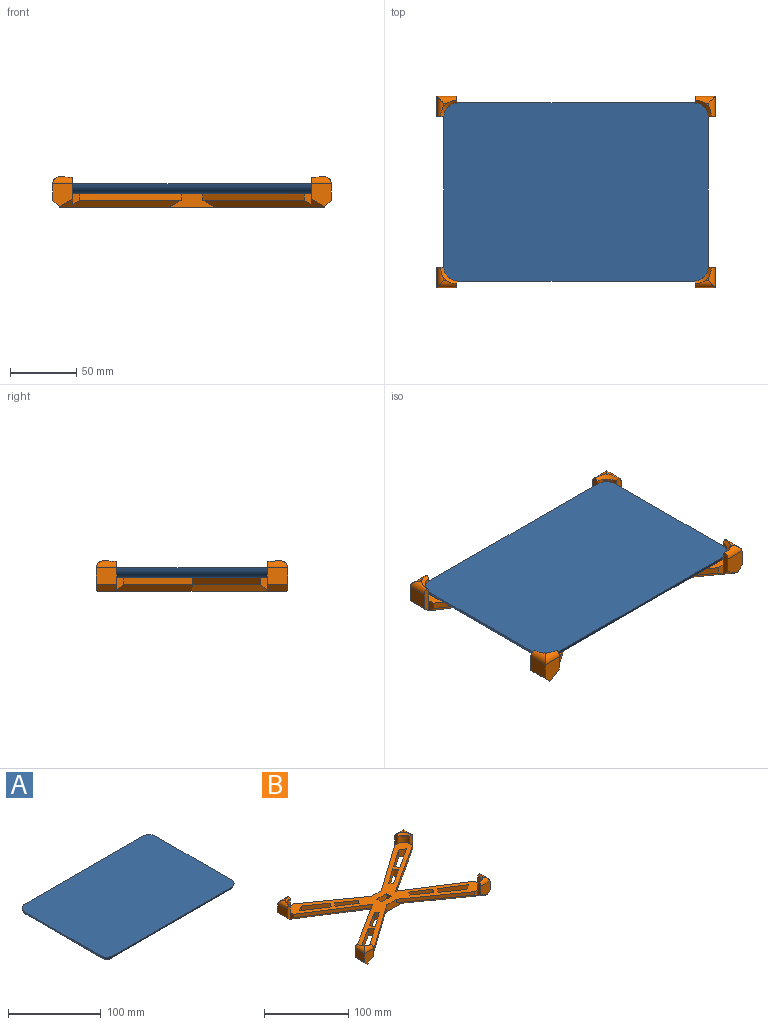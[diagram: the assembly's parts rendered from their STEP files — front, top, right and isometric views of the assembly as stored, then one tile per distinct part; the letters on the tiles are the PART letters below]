
ASSEMBLY  parts=2 mates=1
PART A: 10 faces, bbox 200x135x7.6 mm
  f0: plane 200.03x135mm, normal (0,0,1), area 26920.3mm2, adj f2,f3,f4,f5,f6,f7,f8,f9
  f1: plane 180.35x115.33mm, normal (0,0,-1), area 20798.9mm2, adj f2,f3,f4,f5
  f2: cylinder r=10.16mm len=180.35mm, axis (-1,0,0), area 2415.3mm2, adj f0,f1,f6,f7
  f3: cylinder r=10.16mm len=115.33mm, axis (0,1,0), area 1544.4mm2, adj f0,f1,f6,f8
  f4: cylinder r=10.16mm len=115.33mm, axis (0,1,0), area 1544.4mm2, adj f0,f1,f7,f9
  f5: cylinder r=10.16mm len=180.35mm, axis (-1,0,0), area 2415.3mm2, adj f0,f1,f8,f9
  f6: sphere r=10.16mm, area 121.6mm2, adj f0,f2,f3
  f7: sphere r=10.16mm, area 121.6mm2, adj f0,f2,f4
  f8: sphere r=10.16mm, area 121.6mm2, adj f0,f3,f5
  f9: sphere r=10.16mm, area 121.6mm2, adj f0,f4,f5
PART B: 116 faces, bbox 210.8x144.8x22.9 mm
  f0: plane 200.66x134.62mm, normal (0,0,1), area 6145mm2, adj f1,f2,f3,f4,f5,f6,f7,f8
  f1: plane 10.16x6.11mm, normal (0.82,-0.58,0), area 76.2mm2, adj f0,f2,f70,f71
  f2: plane 32.46x20.8mm, normal (-0.54,-0.84,0), area 391.7mm2, adj f0,f1,f3,f71
  f3: plane 10.16x9.01mm, normal (-0.49,0.87,0), area 105.1mm2, adj f0,f2,f70,f71
  f4: plane 24.65x15.79mm, normal (-0.54,-0.84,0), area 297.4mm2, adj f0,f5,f61,f71
  f5: plane 10.16x5.91mm, normal (-0.82,0.58,0), area 73.6mm2, adj f0,f4,f6,f71
  f6: plane 23.6x16.78mm, normal (0.58,0.82,0), area 294.2mm2, adj f0,f5,f61,f71
  f7: plane 32.59x20.88mm, normal (-0.54,0.84,0), area 393.2mm2, adj f0,f8,f62,f71
  f8: plane 10.16x6.11mm, normal (0.82,0.58,0), area 76.2mm2, adj f0,f7,f9,f71
  f9: plane 27.91x19.84mm, normal (0.58,-0.82,0), area 347.9mm2, adj f0,f8,f62,f71
  f10: plane 10.16x6.11mm, normal (-0.84,-0.54,0), area 73.7mm2, adj f0,f11,f63,f71
  f11: plane 24.53x15.71mm, normal (-0.54,0.84,0), area 295.9mm2, adj f0,f10,f12,f71
  f12: plane 10.16x4.76mm, normal (0.82,0.58,0), area 59.4mm2, adj f0,f11,f63,f71
  f13: plane 10.16x6.31mm, normal (-0.84,0.54,0), area 76.1mm2, adj f0,f14,f64,f71
  f14: plane 32.89x21.07mm, normal (0.54,0.84,0), area 396.9mm2, adj f0,f13,f15,f71
  f15: plane 10.16x9.02mm, normal (0.49,-0.87,0), area 105.2mm2, adj f0,f14,f64,f71
  f16: plane 24.53x15.71mm, normal (0.54,0.84,0), area 295.9mm2, adj f0,f17,f65,f71
  f17: plane 10.16x5.91mm, normal (0.82,-0.58,0), area 73.6mm2, adj f0,f16,f18,f71
  f18: plane 23.71x16.86mm, normal (-0.58,-0.82,0), area 295.6mm2, adj f0,f17,f65,f71
  f19: plane 32.59x20.88mm, normal (0.54,-0.84,0), area 393.2mm2, adj f0,f20,f66,f71
  f20: plane 10.16x6.11mm, normal (-0.82,-0.58,0), area 76.2mm2, adj f0,f19,f21,f71
  f21: plane 27.91x19.84mm, normal (-0.58,0.82,0), area 347.9mm2, adj f0,f20,f66,f71
  f22: plane 10.16x5.91mm, normal (0.82,0.58,0), area 73.6mm2, adj f0,f23,f67,f71
  f23: plane 24.53x15.71mm, normal (0.54,-0.84,0), area 295.9mm2, adj f0,f22,f24,f71
  f24: plane 10.16x4.76mm, normal (-0.82,-0.58,0), area 59.4mm2, adj f0,f23,f67,f71
  f25: plane 10.16x8.01mm, normal (-1,0,0), area 81.4mm2, adj f0,f26,f68,f71
  f26: plane 16.56x10.16mm, normal (0,1,0), area 168.3mm2, adj f0,f25,f27,f71
  f27: plane 10.16x8.01mm, normal (1,0,0), area 81.4mm2, adj f0,f26,f68,f71
  f28: plane 20.27x5.08mm, normal (1,0,0), area 86.4mm2, adj f29,f69,f78,f92,f104,f108
  f29: plane 8.02x5.08mm, normal (0,-1,0), area 33.3mm2, adj f0,f28,f30,f92
  f30: plane 76.81x54.61mm, normal (0.58,-0.82,0), area 478.8mm2, adj f0,f29,f31,f92
  f31: plane 34.1x10.16mm, normal (0,-1,0), area 212.8mm2, adj f0,f30,f32,f71,f92,f99
  f32: plane 76.81x54.61mm, normal (-0.58,-0.82,0), area 478.8mm2, adj f0,f31,f33,f99
  f33: plane 8.02x5.08mm, normal (0,-1,0), area 33.3mm2, adj f0,f32,f34,f99
  f34: plane 20.27x5.08mm, normal (-1,0,0), area 86.4mm2, adj f33,f35,f76,f99,f105,f111
  f35: plane 17.53x15.24mm, normal (0,-1,0), area 224.2mm2, adj f34,f36,f99,f101,f111
  f36: plane 15.24x12.7mm, normal (1,0,0), area 193.5mm2, adj f35,f37,f101,f110
  f37: plane 21.61x5.08mm, normal (0,1,0), area 94.2mm2, adj f36,f38,f76,f97,f101,f105,f110
  f38: plane 9.36x5.08mm, normal (1,0,0), area 36.7mm2, adj f0,f37,f39,f97
  f39: plane 81.28x52.07mm, normal (0.54,0.84,0), area 490.4mm2, adj f0,f38,f40,f97
  f40: plane 81.28x52.07mm, normal (0.54,-0.84,0), area 490.4mm2, adj f0,f39,f41,f98
  f41: plane 9.36x5.08mm, normal (1,0,0), area 36.7mm2, adj f0,f40,f42,f98
  f42: plane 21.61x5.08mm, normal (0,-1,0), area 94.2mm2, adj f41,f43,f74,f98,f100,f107,f112
  f43: plane 15.24x12.7mm, normal (1,0,0), area 193.5mm2, adj f42,f44,f100,f112
  f44: plane 17.53x15.24mm, normal (0,1,0), area 224.2mm2, adj f43,f45,f96,f100,f113
  f45: plane 20.27x5.08mm, normal (-1,0,0), area 86.4mm2, adj f44,f46,f74,f96,f107,f113
  f46: plane 8.02x5.08mm, normal (0,1,0), area 33.3mm2, adj f0,f45,f47,f96
  f47: plane 76.81x54.61mm, normal (-0.58,0.82,0), area 478.8mm2, adj f0,f46,f48,f96
  f48: plane 34.1x10.16mm, normal (0,1,0), area 212.8mm2, adj f0,f47,f49,f71,f95,f96
  f49: plane 76.81x54.61mm, normal (0.58,0.82,0), area 478.8mm2, adj f0,f48,f50,f95
  f50: plane 8.02x5.08mm, normal (0,1,0), area 33.3mm2, adj f0,f49,f51,f95
  f51: plane 20.27x5.08mm, normal (1,0,0), area 86.4mm2, adj f50,f52,f72,f95,f106,f115
  f52: plane 17.53x15.24mm, normal (0,1,0), area 224.2mm2, adj f51,f53,f95,f103,f115
  f53: plane 15.24x12.7mm, normal (-1,0,0), area 193.5mm2, adj f52,f54,f103,f114
  f54: plane 21.61x5.08mm, normal (0,-1,0), area 94.2mm2, adj f53,f55,f72,f93,f103,f106,f114
  f55: plane 9.36x5.08mm, normal (-1,0,0), area 36.7mm2, adj f0,f54,f56,f93
  f56: plane 81.28x52.07mm, normal (-0.54,-0.84,0), area 490.4mm2, adj f0,f55,f57,f93
  f57: plane 81.28x52.07mm, normal (-0.54,0.84,0), area 490.4mm2, adj f0,f56,f58,f94
  f58: plane 9.36x5.08mm, normal (-1,0,0), area 36.7mm2, adj f0,f57,f59,f94
  f59: plane 21.61x5.08mm, normal (0,1,0), area 94.2mm2, adj f58,f60,f78,f94,f102,f104,f109
  f60: plane 15.24x12.7mm, normal (-1,0,0), area 193.5mm2, adj f59,f69,f102,f109
  f61: plane 10.16x4.92mm, normal (0.84,-0.54,0), area 59.4mm2, adj f0,f4,f6,f71
  f62: plane 10.16x9.02mm, normal (-0.49,-0.87,0), area 105.2mm2, adj f0,f7,f9,f71
  f63: plane 24x17.06mm, normal (0.58,-0.82,0), area 299.1mm2, adj f0,f10,f12,f71
  f64: plane 27.91x19.84mm, normal (-0.58,-0.82,0), area 347.9mm2, adj f0,f13,f15,f71
  f65: plane 10.16x4.76mm, normal (-0.82,0.58,0), area 59.4mm2, adj f0,f16,f18,f71
  f66: plane 10.16x9.02mm, normal (0.49,0.87,0), area 105.2mm2, adj f0,f19,f21,f71
  f67: plane 23.71x16.86mm, normal (-0.58,0.82,0), area 295.6mm2, adj f0,f22,f24,f71
  f68: plane 16.56x10.16mm, normal (0,-1,0), area 168.3mm2, adj f0,f25,f27,f71
  f69: plane 17.53x15.24mm, normal (0,-1,0), area 224.2mm2, adj f28,f60,f92,f102,f108
  f70: plane 27.8x19.77mm, normal (0.58,0.82,0), area 346.6mm2, adj f0,f1,f3,f71
  f71: plane 200.66x143.82mm, normal (0,0,-1), area 2303.1mm2, adj f1,f2,f3,f4,f5,f6,f7,f8
  f72: cylinder r=10.16mm len=10.16mm, axis (0,0,-1), area 154.2mm2, adj f0,f51,f54,f80,f81,f91,f106
  f73: plane 2.54x2.54mm, normal (0,0,1), area 2.9mm2, adj f106,f114,f115
  f74: cylinder r=10.16mm len=10.16mm, axis (0,0,-1), area 154.2mm2, adj f0,f42,f45,f82,f83,f90,f107
  f75: plane 2.54x2.54mm, normal (0,0,1), area 2.9mm2, adj f107,f112,f113
  f76: cylinder r=10.16mm len=10.16mm, axis (0,0,-1), area 154.2mm2, adj f0,f34,f37,f84,f85,f89,f105
  f77: plane 2.54x2.54mm, normal (0,0,1), area 2.9mm2, adj f105,f110,f111
  f78: cylinder r=10.16mm len=10.16mm, axis (0,0,-1), area 154.2mm2, adj f0,f28,f59,f86,f87,f88,f104
  f79: plane 2.54x2.54mm, normal (0,0,1), area 2.9mm2, adj f104,f108,f109
  f80: plane 3.72x3.72mm, normal (0.71,-0.71,0), area 6.7mm2, adj f72,f81,f91
  f81: plane 3.72x3.72mm, normal (0,0,-1), area 1.2mm2, adj f72,f80
  f82: plane 3.72x3.72mm, normal (-0.71,-0.71,0), area 6.7mm2, adj f74,f83,f90
  f83: plane 3.72x3.72mm, normal (0,0,-1), area 1.2mm2, adj f74,f82
  f84: plane 3.72x3.72mm, normal (-0.71,0.71,0), area 6.7mm2, adj f76,f85,f89
  f85: plane 3.72x3.72mm, normal (0,0,-1), area 1.2mm2, adj f76,f84
  f86: plane 3.72x3.72mm, normal (0.71,0.71,0), area 6.7mm2, adj f78,f87,f88
  f87: plane 3.72x3.72mm, normal (0,0,-1), area 1.2mm2, adj f78,f86
  f88: plane 3.72x3.72mm, normal (0.5,0.5,0.71), area 1.7mm2, adj f78,f86
  f89: plane 3.72x3.72mm, normal (-0.5,0.5,0.71), area 1.7mm2, adj f76,f84
  f90: plane 3.72x3.72mm, normal (-0.5,-0.5,0.71), area 1.7mm2, adj f74,f82
  f91: plane 3.72x3.72mm, normal (0.5,-0.5,0.71), area 1.7mm2, adj f72,f80
  f92: plane 92.3x59.69mm, normal (0.41,-0.58,-0.71), area 729.1mm2, adj f28,f29,f30,f31,f69,f71,f102
  f93: plane 92.44x58.1mm, normal (-0.38,-0.6,-0.71), area 734.8mm2, adj f54,f55,f56,f71,f94,f103
  f94: plane 92.44x58.1mm, normal (-0.38,0.6,-0.71), area 734.8mm2, adj f57,f58,f59,f71,f93,f102
  f95: plane 92.3x59.69mm, normal (0.41,0.58,-0.71), area 729.1mm2, adj f48,f49,f50,f51,f52,f71,f103
  f96: plane 92.3x59.69mm, normal (-0.41,0.58,-0.71), area 729.1mm2, adj f44,f45,f46,f47,f48,f71,f100
  f97: plane 92.44x58.1mm, normal (0.38,0.6,-0.71), area 734.8mm2, adj f37,f38,f39,f71,f98,f101
  f98: plane 92.44x58.1mm, normal (0.38,-0.6,-0.71), area 734.8mm2, adj f40,f41,f42,f71,f97,f100
  f99: plane 92.3x59.69mm, normal (-0.41,-0.58,-0.71), area 729.1mm2, adj f31,f32,f33,f34,f35,f71,f101
  f100: plane 15.24x5.08mm, normal (0.71,0,-0.71), area 108.2mm2, adj f42,f43,f44,f71,f96,f98
  f101: plane 15.24x5.08mm, normal (0.71,0,-0.71), area 108.2mm2, adj f35,f36,f37,f71,f97,f99
  f102: plane 15.24x5.08mm, normal (-0.71,0,-0.71), area 108.2mm2, adj f59,f60,f69,f71,f92,f94
  f103: plane 15.24x5.08mm, normal (-0.71,0,-0.71), area 108.2mm2, adj f52,f53,f54,f71,f93,f95
  f104: cone r=10.16mm half-angle=45deg, axis (0,0,1), area 58.8mm2, adj f28,f59,f78,f79,f108,f109
  f105: cone r=10.16mm half-angle=45deg, axis (0,0,1), area 58.8mm2, adj f34,f37,f76,f77,f110,f111
  f106: cone r=10.16mm half-angle=45deg, axis (0,0,1), area 58.8mm2, adj f51,f54,f72,f73,f114,f115
  f107: cone r=10.16mm half-angle=45deg, axis (0,0,1), area 58.8mm2, adj f42,f45,f74,f75,f112,f113
  f108: cylinder r=5.08mm len=15.24mm, axis (1,0,0), area 95.5mm2, adj f28,f69,f79,f104,f109
  f109: cylinder r=5.08mm len=15.24mm, axis (0,-1,0), area 95.5mm2, adj f59,f60,f79,f104,f108
  f110: cylinder r=5.08mm len=15.24mm, axis (0,1,0), area 95.5mm2, adj f36,f37,f77,f105,f111
  f111: cylinder r=5.08mm len=15.24mm, axis (1,0,0), area 95.5mm2, adj f34,f35,f77,f105,f110
  f112: cylinder r=5.08mm len=15.24mm, axis (0,1,0), area 95.5mm2, adj f42,f43,f75,f107,f113
  f113: cylinder r=5.08mm len=15.24mm, axis (-1,0,0), area 95.5mm2, adj f44,f45,f75,f107,f112
  f114: cylinder r=5.08mm len=15.24mm, axis (0,-1,0), area 95.5mm2, adj f53,f54,f73,f106,f115
  f115: cylinder r=5.08mm len=15.24mm, axis (-1,0,0), area 95.5mm2, adj f51,f52,f73,f106,f114
PLACE A t=(-30.41,-18.45,-7.21)mm
PLACE B t=(-30.42,-18.43,-7.21)mm
MATE fastened B.f0 <-> A.f1  axis (0,0,1) through (-30.41,-18.45,-7.21)mm
